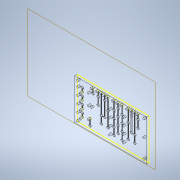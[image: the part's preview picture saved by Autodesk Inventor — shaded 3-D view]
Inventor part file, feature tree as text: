
AUTODESK INVENTOR PART (.ipt)
format: ipt  version: 2021 (Build 250183000, 183)  size: 466,432 bytes
history: native  units: in
note: dims shown in document units (in); Inventor stores cm internally (conversion verified against a paired STEP export)
features: reference x60, projected_geometry x16, other x10, extrude x3, hole x3, sketch x2, plane x1
ambient origin geometry x8: Origin, YZ Plane, XZ Plane, XY Plane, X Axis, Y Axis, Z Axis, Center Point
bodies: Solid1 (feature_tree)
feature tree (95):
  extrude  "Extrusion base plate"  [1 undecoded]
  plane  "work plane for rib creation"
  other  "channels as rib"
  extrude  "extrusion of ribs to get cutout"  Depth=0.315in
  extrude  "valve space extrusion"  Depth=0.9055in
  other  "all valve spaces"
  other  "projected points for every hole for control layer only"
  hole  "holes for control layer"  [1 undecoded]
  other  "projected points for every hole for flow layer only"
  hole  "holes for connection to flow layer"  [1 undecoded]
  hole  "holes in corners"  [1 undecoded]
  other  "all holes for flow layer only"
  sketch  "Sketch1"  dims[d2=0.2362in d3=0.0in d4=-0.0394in]
  other  "channels and points for valves and for connectors for control layer"
  reference  "Reference1"
  reference  "Reference2"
  reference  "Reference3"
  reference  "Reference4"
  reference  "Reference5"
  reference  "Reference6"
  reference  "Reference7"
  reference  "Reference8"
  reference  "Reference9"
  reference  "Reference10"
  reference  "Reference11"
  reference  "Reference12"
  reference  "Reference13"
  reference  "Reference14"
  reference  "Reference15"
  reference  "Reference16"
  reference  "Reference17"
  reference  "Reference18"
  reference  "Reference19"
  reference  "Reference20"
  reference  "Reference21"
  reference  "Reference22"
  reference  "Reference23"
  reference  "Reference24"
  reference  "Reference25"
  reference  "Reference26"
  reference  "Reference27"
  reference  "Reference28"
  reference  "Reference29"
  reference  "Reference30"
  reference  "Reference31"
  reference  "Reference32"
  reference  "Reference33"
  reference  "Reference34"
  reference  "Reference35"
  sketch  "Sketch3"  dims[d5=7.874in d6=11.811in d7=0.9055in d9=0.3543in d10=0.3543in d11=0.3543in d12=0.3543in d19=0.0394in d20=0.0394in d21=0.0in d22=0.0in d23=0.0394in d24=0.0in d25=0.1024in d26=0.0in d27=0.063in d28=0.0in d29=0.1654in d30=0.2362in d31=0.1575in d32=0.0787in d33=90.0deg d34=0.0394in d35=0.0in d36=0.1654in d37=0.2362in d38=0.1575in d39=0.0787in d40=90.0deg d41=0.0394in d42=0.0in d43=0.1772in d44=0.2362in d45=0.1575in d46=0.0787in d47=90.0deg d48=0.315in d49=0.8108in d50=0.1181in d51=0.0886in d52=0.315in]
  projected_geometry  "Projected Loop1"
  projected_geometry  "Projected Loop2"
  projected_geometry  "Projected Loop3"
  projected_geometry  "Projected Loop4"
  projected_geometry  "Projected Loop5"
  projected_geometry  "Projected Loop6"
  projected_geometry  "Projected Loop7"
  projected_geometry  "Projected Loop8"
  projected_geometry  "Projected Loop9"
  projected_geometry  "Projected Loop10"
  projected_geometry  "Projected Loop11"
  projected_geometry  "Projected Loop12"
  projected_geometry  "Projected Loop13"
  projected_geometry  "Projected Loop14"
  projected_geometry  "Projected Loop15"
  projected_geometry  "Projected Loop16"
  reference  "Reference36"
  other  "Projected points for every valve"
  reference  "Reference37"
  reference  "Reference38"
  reference  "Reference39"
  reference  "Reference40"
  reference  "Reference41"
  reference  "Reference42"
  reference  "Reference43"
  reference  "Reference44"
  reference  "Reference45"
  reference  "Reference46"
  reference  "Reference47"
  reference  "Reference48"
  reference  "Reference49"
  reference  "Reference50"
  reference  "Reference51"
  reference  "Reference52"
  reference  "Reference53"
  reference  "Reference54"
  reference  "Reference55"
  reference  "Reference56"
  other  "projection for holes in corners"
  reference  "Reference57"
  reference  "Reference58"
  reference  "Reference59"
  reference  "Reference60"
  other  "Millifluidic Board.iam"
  other  "Flow Layer:1"
note: 4 required parameter values undecoded (feature->parameter linkage not recoverable at this tier; creation-order binding heuristic only, values carry confidence <= 0.55)
